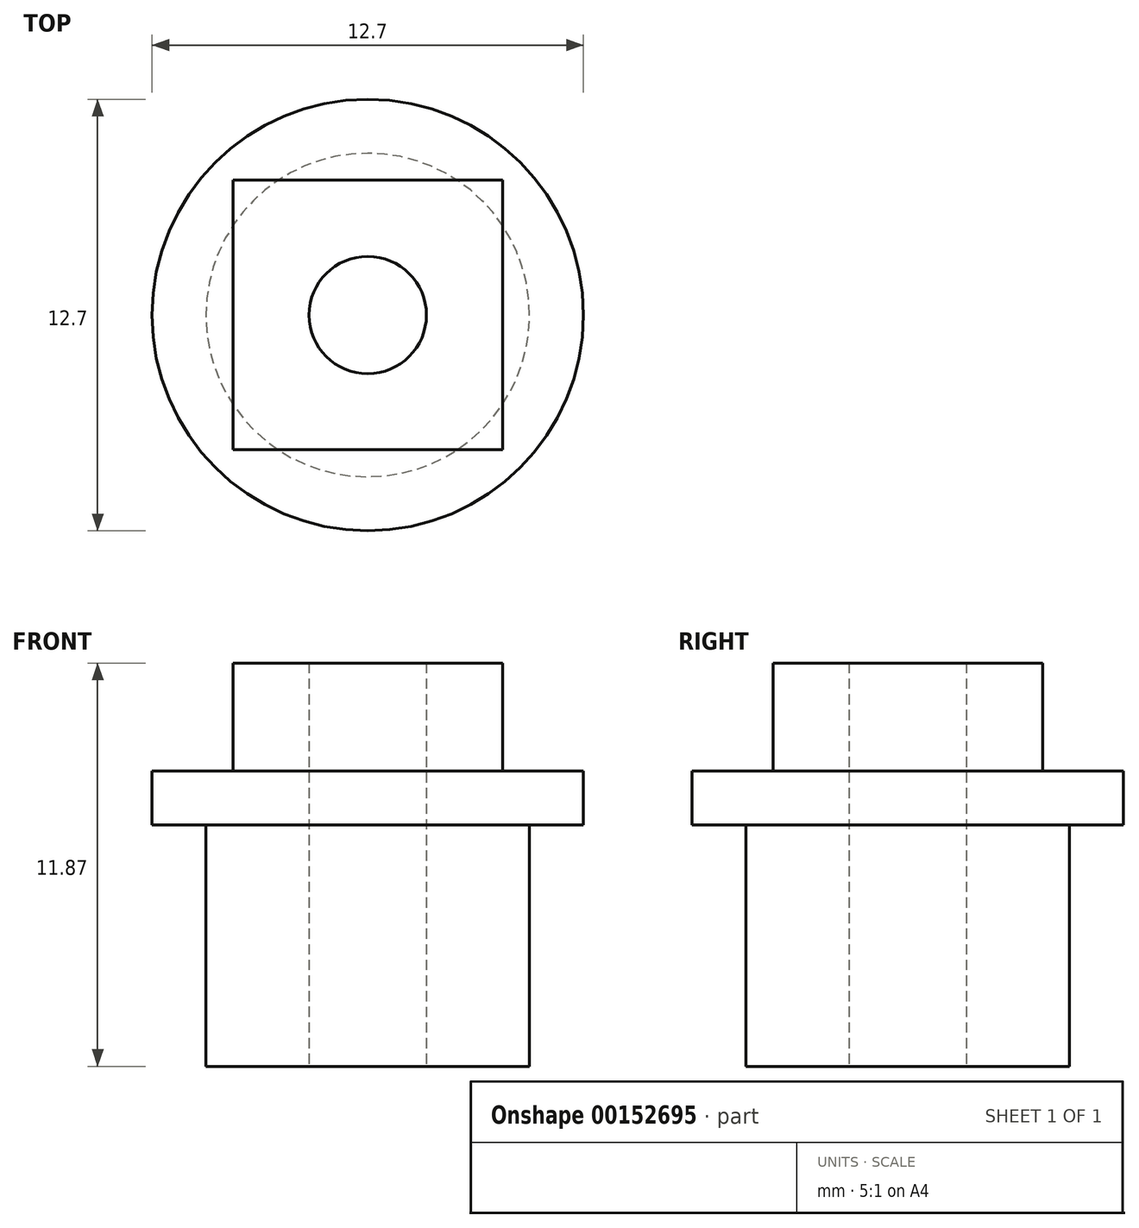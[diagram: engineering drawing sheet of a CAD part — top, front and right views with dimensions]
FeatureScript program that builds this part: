
annotation { "Feature Type Name" : "Feature", "Feature Type Description" : "" }
export const myFeature = defineFeature(function(context is Context, id is Id, definition is map)
    precondition{}
    {
        {
            var Q0;
            Q0=qCreatedBy(makeId("Top.planeOp"),FACE);
            var sketch = newSketch(context, id + "F0", { "sketchPlane" : qUnion([Q0])});
            skCircle(sketch, "E0", {"center": v(0, 0) * mm, "radius": 1.73 * mm});
            skCircle(sketch, "E1", {"center": v(0, 0) * mm, "radius": 4.76 * mm});
            skSolve(sketch);
        }
        {
            var Q0;
            Q0 = qSketchRegion(id + "F0", true);
            extrude(context, id + "F1", {"entities" : qUnion([Q0]), "depth" : 7.11 * mm});
        }
        {
            var Q0;
            Q0=makeQuery(id+"F1.opExtrude","CAP_FACE",FACE,{"disambiguationData":[OSD([sQuery(id+"F0.wireOp",EDGE,"E0"),sQuery(id+"F0.wireOp",EDGE,"E1")])],"isStart":false});
            var sketch = newSketch(context, id + "F2", { "sketchPlane" : qUnion([Q0])});
            skCircle(sketch, "E2", {"center": v(0, 0) * mm, "radius": 1.73 * mm});
            skCircle(sketch, "E3", {"center": v(0, 0) * mm, "radius": 6.35 * mm});
            skSolve(sketch);
        }
        {
            var Q0;
            Q0 = qSketchRegion(id + "F2", true);
            extrude(context, id + "F3", {"entities" : qUnion([Q0]), "operationType" : NewBodyOperationType.ADD, "depth" : 1.59 * mm});
        }
        {
            var Q0;
            Q0=makeQuery(id+"F3.opExtrude","CAP_FACE",FACE,{"disambiguationData":[OSD([sQuery(id+"F2.wireOp",EDGE,"E2"),sQuery(id+"F2.wireOp",EDGE,"E3")])],"isStart":false});
            var sketch = newSketch(context, id + "F4", { "sketchPlane" : qUnion([Q0])});
            skCircle(sketch, "E4", {"center": v(0, 0) * mm, "radius": 1.73 * mm});
            skLineSegment(sketch, "E5.bottom", {"start": v(3.97, -3.97) * mm, "end": v(-3.97, -3.97) * mm});
            skLineSegment(sketch, "E5.top", {"start": v(3.97, 3.97) * mm, "end": v(-3.97, 3.97) * mm});
            skLineSegment(sketch, "E5.left", {"start": v(3.97, -3.97) * mm, "end": v(3.97, 3.97) * mm});
            skLineSegment(sketch, "E5.right", {"start": v(-3.97, -3.97) * mm, "end": v(-3.97, 3.97) * mm});
            skSolve(sketch);
        }
        {
            var Q0;
            Q0 = qSketchRegion(id + "F4", true);
            extrude(context, id + "F5", {"entities" : qUnion([Q0]), "operationType" : NewBodyOperationType.ADD, "depth" : 3.17 * mm});
        }
    });
